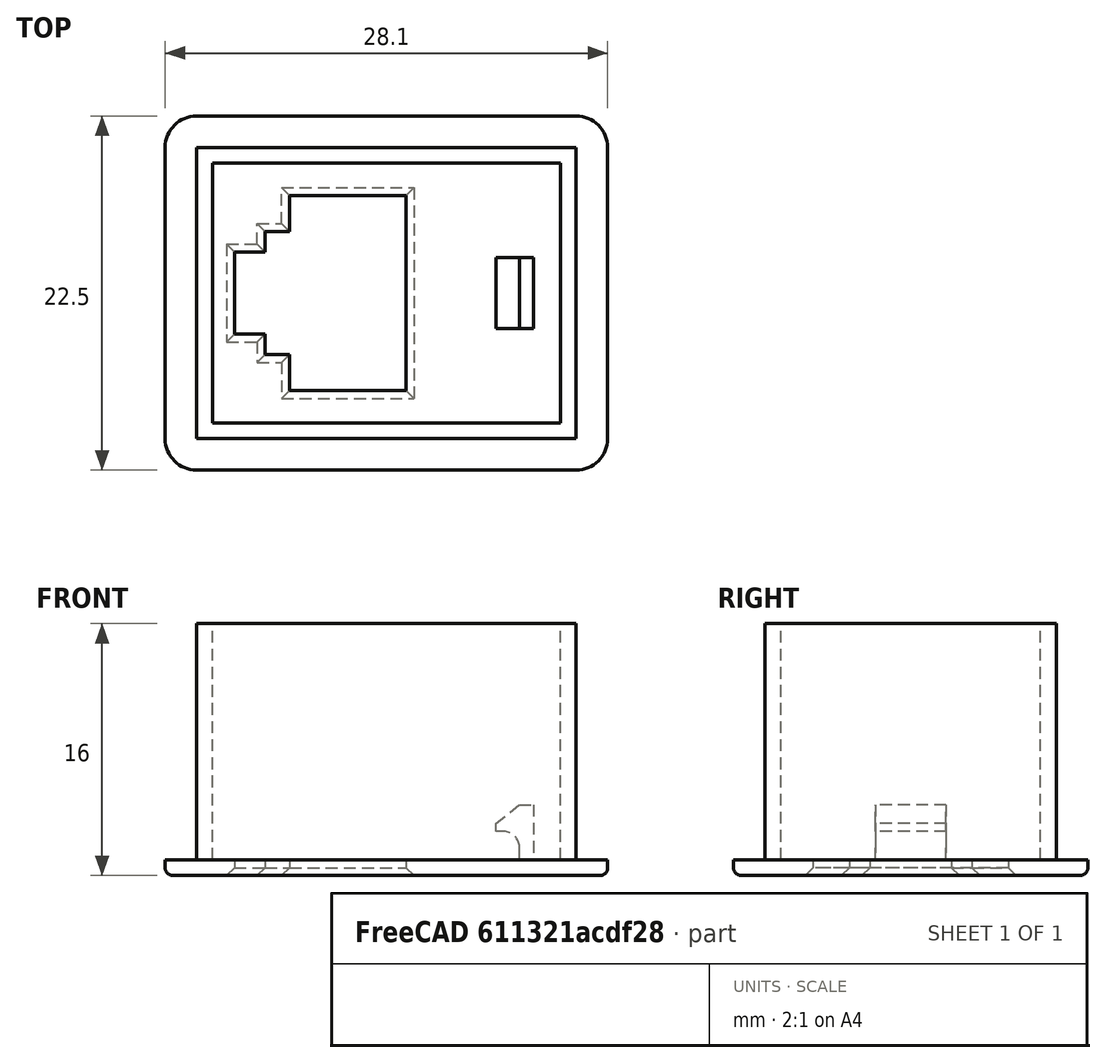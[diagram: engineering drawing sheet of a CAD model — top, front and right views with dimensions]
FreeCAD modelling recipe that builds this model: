
FCSTD DOCUMENT  (FreeCAD 0.17RUnknown)
Label: test202_lanport
License: All rights reserved
LicenseURL: http://en.wikipedia.org/wiki/All_rights_reserved
objects: Sketcher::SketchObject×5, PartDesign::Pad×3, PartDesign::Plane×2, PartDesign::Fillet×1, PartDesign::Chamfer×1, PartDesign::Body×1, Mesh::Feature×1, Mesh::Curvature×1
note: 16 computed .brp shape members not serialized (recipe doc carries the construction recipe); baked Part::Feature solids carry a one-line shape summary decoded from their .brp

FEATURE [Sketcher::SketchObject] Sketch  label="LanChanger"
  MapMode = 5
  Support = -> [XY_Plane]
  sketch-geometry (24):
    g0: LineSegment [constr] StartX=-5.25 StartY=6 StartZ=0 EndX=5.25 EndY=6 EndZ=0
    g1: LineSegment [constr] StartX=5.25 StartY=6 StartZ=0 EndX=5.25 EndY=-6 EndZ=0
    g2: LineSegment [constr] StartX=5.25 StartY=-6 StartZ=0 EndX=-5.25 EndY=-6 EndZ=0
    g3: LineSegment [constr] StartX=-5.25 StartY=-6 StartZ=0 EndX=-5.25 EndY=6 EndZ=0
    g4: LineSegment StartX=-1.75 StartY=6 StartZ=0 EndX=5.25 EndY=6 EndZ=0
    g5: LineSegment StartX=-1.75 StartY=6 StartZ=0 EndX=-1.75 EndY=3.7 EndZ=0
    g6: LineSegment StartX=-1.75 StartY=3.7 StartZ=0 EndX=-3.3 EndY=3.7 EndZ=0
    g7: LineSegment StartX=-3.3 StartY=3.7 StartZ=0 EndX=-3.3 EndY=2.4 EndZ=0
    g8: LineSegment StartX=-3.3 StartY=2.4 StartZ=0 EndX=-5.25 EndY=2.4 EndZ=0
    g9: LineSegment StartX=-1.75 StartY=-3.7 StartZ=0 EndX=-3.3 EndY=-3.7 EndZ=0
    g10: LineSegment StartX=-3.3 StartY=-3.7 StartZ=0 EndX=-3.3 EndY=-2.4 EndZ=0
    g11: LineSegment StartX=-3.3 StartY=-2.4 StartZ=0 EndX=-5.25 EndY=-2.4 EndZ=0
    g12: LineSegment StartX=-1.75 StartY=-6 StartZ=0 EndX=5.25 EndY=-6 EndZ=0
    g13: LineSegment StartX=-1.75 StartY=-6 StartZ=0 EndX=-1.75 EndY=-3.7 EndZ=0
    g14: LineSegment StartX=-5.25 StartY=-2.4 StartZ=0 EndX=-5.25 EndY=2.4 EndZ=0
    g15: LineSegment StartX=5.25 StartY=6 StartZ=0 EndX=5.25 EndY=-6 EndZ=0
    g16: LineSegment StartX=-6.65 StartY=8.05 StartZ=0 EndX=15.05 EndY=8.05 EndZ=0
    g17: LineSegment StartX=15.05 StartY=8.05 StartZ=0 EndX=15.05 EndY=-8.05 EndZ=0
    g18: LineSegment StartX=15.05 StartY=-8.05 StartZ=0 EndX=-6.65 EndY=-8.05 EndZ=0
    g19: LineSegment StartX=-6.65 StartY=-8.05 StartZ=0 EndX=-6.65 EndY=8.05 EndZ=0
    g20: LineSegment StartX=11.65 StartY=2.45 StartZ=0 EndX=13.75 EndY=2.45 EndZ=0
    g21: LineSegment StartX=13.75 StartY=2.45 StartZ=0 EndX=13.75 EndY=-2.45 EndZ=0
    g22: LineSegment StartX=13.75 StartY=-2.45 StartZ=0 EndX=11.65 EndY=-2.45 EndZ=0
    g23: LineSegment StartX=11.65 StartY=-2.45 StartZ=0 EndX=11.65 EndY=2.45 EndZ=0
  constraints (69):
    c: Coincident(g0,g1)
    c: Coincident(g1,g2)
    c: Coincident(g2,g3)
    c: Coincident(g3,g0)
    c: Horizontal(g0)
    c: Horizontal(g2)
    c: Vertical(g1)
    c: Vertical(g3)
    c: Symmetric(g0,g1,g-1)
    c: Distance(g1) = 12
    c: Distance(g0) = 10.5
    c: PointOnObject(g4,g0)
    c: Coincident(g4,g0)
    c: Distance(g4) = 7
    c: Coincident(g4,g5)
    c: Vertical(g5)
    c: Coincident(g5,g6)
    c: Horizontal(g6)
    c: Coincident(g6,g7)
    c: Vertical(g7)
    c: Coincident(g7,g8)
    c: PointOnObject(g8,g3)
    c: Horizontal(g8)
    c: Distance(g5) = 2.3
    c: Distance(g6) = 1.55
    c: Distance(g7) = 1.3
    c: Distance(g12) = 7
    c: Coincident(g12,g13)
    c: Vertical(g13)
    c: Coincident(g13,g9)
    c: Horizontal(g9)
    c: Coincident(g9,g10)
    c: Vertical(g10)
    c: Coincident(g10,g11)
    c: Horizontal(g11)
    c: Distance(g13) = 2.3
    c: Distance(g9) = 1.55
    c: Distance(g10) = 1.3
    c: Coincident(g14,g11)
    c: Coincident(g14,g8)
    c: Coincident(g15,g0)
    c: Coincident(g15,g1)
    c: Coincident(g12,g1)
    c: PointOnObject(g12,g2)
    c: PointOnObject(g14,g3)
    c: Coincident(g16,g17)
    c: Coincident(g17,g18)
    c: Coincident(g18,g19)
    c: Coincident(g19,g16)
    c: Horizontal(g16)
    c: Horizontal(g18)
    c: Vertical(g17)
    c: Vertical(g19)
    c: Symmetric(g16,g18,g-1)
    c: Distance(g16) = 21.7
    c: Distance(g8,g19) = 1.4
    c: Distance(g19) = 16.1
    c: Coincident(g20,g21)
    c: Coincident(g21,g22)
    c: Coincident(g22,g23)
    c: Coincident(g23,g20)
    c: Horizontal(g20)
    c: Horizontal(g22)
    c: Vertical(g21)
    c: Vertical(g23)
    c: Symmetric(g22,g20,g-1)
    c: Distance(g20,g17) = 1.3
    c: Distance(g20) = 2.1
    c: Distance(g21) = 4.9
FEATURE [Sketcher::SketchObject] Sketch001
  ExternalGeometry = -> [Sketch]
  MapMode = 5
  Support = -> [XY_Plane]
  sketch-geometry (8):
    g0: LineSegment StartX=-7.85 StartY=9.25 StartZ=0 EndX=16.25 EndY=9.25 EndZ=0
    g1: LineSegment StartX=16.25 StartY=9.25 StartZ=0 EndX=16.25 EndY=-9.25 EndZ=0
    g2: LineSegment StartX=16.25 StartY=-9.25 StartZ=0 EndX=-7.85 EndY=-9.25 EndZ=0
    g3: LineSegment StartX=-7.85 StartY=-9.25 StartZ=0 EndX=-7.85 EndY=9.25 EndZ=0
    g4: LineSegment StartX=-6.85 StartY=8.25 StartZ=0 EndX=15.25 EndY=8.25 EndZ=0
    g5: LineSegment StartX=15.25 StartY=8.25 StartZ=0 EndX=15.25 EndY=-8.25 EndZ=0
    g6: LineSegment StartX=15.25 StartY=-8.25 StartZ=0 EndX=-6.85 EndY=-8.25 EndZ=0
    g7: LineSegment StartX=-6.85 StartY=-8.25 StartZ=0 EndX=-6.85 EndY=8.25 EndZ=0
  constraints (24):
    c: Coincident(g0,g1)
    c: Coincident(g1,g2)
    c: Coincident(g2,g3)
    c: Coincident(g3,g0)
    c: Horizontal(g0)
    c: Horizontal(g2)
    c: Vertical(g1)
    c: Vertical(g3)
    c: Coincident(g4,g5)
    c: Coincident(g5,g6)
    c: Coincident(g6,g7)
    c: Coincident(g7,g4)
    c: Horizontal(g4)
    c: Horizontal(g6)
    c: Vertical(g5)
    c: Vertical(g7)
    c: Distance(g4,g1) = 1
    c: Symmetric(g4,g5,g-1)
    c: Distance(g-3,g4) = 0.2
    c: Distance(g-4,g7) = 0.2
    c: Distance(g-3,g5) = 0.2
    c: Distance(g4,g0) = 1
    c: Symmetric(g0,g1,g-1)
    c: Distance(g4,g3) = 1
FEATURE [PartDesign::Pad] Pad
  Length = 15
  Length2 = 100
  Profile = -> Sketch001
  Type = 0
FEATURE [Sketcher::SketchObject] Sketch002
  ExternalGeometry = -> [Pad,Sketch]
  MapMode = 5
  Placement = pos=(0,0,0) rot=(1,0,0;3.14159rad)
  Support = -> [Pad]
  sketch-geometry (20):
    g0: LineSegment StartX=-7.85 StartY=11.25 StartZ=0 EndX=16.25 EndY=11.25 EndZ=0
    g1: LineSegment StartX=18.25 StartY=9.25 StartZ=0 EndX=18.25 EndY=-9.25 EndZ=0
    g2: LineSegment StartX=16.25 StartY=-11.25 StartZ=0 EndX=-7.85 EndY=-11.25 EndZ=0
    g3: LineSegment StartX=-9.85 StartY=-9.25 StartZ=0 EndX=-9.85 EndY=9.25 EndZ=0
    g4: ArcOfCircle CenterX=-7.85 CenterY=9.25 CenterZ=0 NormalX=0 NormalY=0 NormalZ=1 AngleXU=0 Radius=2 StartAngle=1.5708 EndAngle=3.14159
    g5: ArcOfCircle CenterX=16.25 CenterY=9.25 CenterZ=0 NormalX=0 NormalY=0 NormalZ=1 AngleXU=0 Radius=2 StartAngle=0 EndAngle=1.5708
    g6: ArcOfCircle CenterX=16.25 CenterY=-9.25 CenterZ=0 NormalX=0 NormalY=0 NormalZ=1 AngleXU=0 Radius=2 StartAngle=4.71239 EndAngle=6.28319
    g7: ArcOfCircle CenterX=-7.85 CenterY=-9.25 CenterZ=0 NormalX=0 NormalY=0 NormalZ=1 AngleXU=0 Radius=2 StartAngle=3.14159 EndAngle=4.71239
    g8: LineSegment StartX=-5.45 StartY=2.6 StartZ=0 EndX=-3.5 EndY=2.6 EndZ=0
    g9: LineSegment StartX=-3.5 StartY=2.6 StartZ=0 EndX=-3.5 EndY=3.9 EndZ=0
    g10: LineSegment StartX=-3.5 StartY=3.9 StartZ=0 EndX=-1.95 EndY=3.9 EndZ=0
    g11: LineSegment StartX=-1.95 StartY=3.9 StartZ=0 EndX=-1.95 EndY=6.2 EndZ=0
    g12: LineSegment StartX=-1.95 StartY=6.2 StartZ=0 EndX=5.45 EndY=6.2 EndZ=0
    g13: LineSegment StartX=-5.45 StartY=-2.6 StartZ=0 EndX=-3.5 EndY=-2.6 EndZ=0
    g14: LineSegment StartX=-3.5 StartY=-2.6 StartZ=0 EndX=-3.5 EndY=-3.9 EndZ=0
    g15: LineSegment StartX=-3.5 StartY=-3.9 StartZ=0 EndX=-1.95 EndY=-3.9 EndZ=0
    g16: LineSegment StartX=-1.95 StartY=-3.9 StartZ=0 EndX=-1.95 EndY=-6.2 EndZ=0
    g17: LineSegment StartX=-1.95 StartY=-6.2 StartZ=0 EndX=5.45 EndY=-6.2 EndZ=0
    g18: LineSegment StartX=-5.45 StartY=-2.6 StartZ=0 EndX=-5.45 EndY=2.6 EndZ=0
    g19: LineSegment StartX=5.45 StartY=-6.2 StartZ=0 EndX=5.45 EndY=6.2 EndZ=0
  constraints (53):
    c: Horizontal(g0)
    c: Horizontal(g2)
    c: Vertical(g1)
    c: Vertical(g3)
    c: Tangent(g3,g4) = 1.5708
    c: Tangent(g0,g4) = 1.5708
    c: Tangent(g0,g5) = 1.5708
    c: Tangent(g1,g5) = 1.5708
    c: Tangent(g1,g6) = 1.5708
    c: Tangent(g2,g6) = 1.5708
    c: Tangent(g2,g7) = 1.5708
    c: Tangent(g3,g7) = 1.5708
    c: Radius(g4) = 2
    c: Equal(g4,g5)
    c: Equal(g4,g6)
    c: Equal(g4,g7)
    c: Coincident(g5,g-3)
    c: Coincident(g7,g-4)
    c: Horizontal(g8)
    c: Coincident(g8,g9)
    c: Vertical(g9)
    c: Coincident(g9,g10)
    c: Coincident(g10,g11)
    c: Coincident(g11,g12)
    c: Horizontal(g12)
    c: Vertical(g11)
    c: Horizontal(g10)
    c: Equal(g-6,g8)
    c: Equal(g10,g-5)
    c: Equal(g-8,g9)
    c: Equal(g-9,g11)
    c: DistanceX(g11,g-9) = 0.2
    c: DistanceY(g-9,g11) = 0.2
    c: Horizontal(g13)
    c: Coincident(g13,g14)
    c: Vertical(g14)
    c: Coincident(g14,g15)
    c: Coincident(g15,g16)
    c: Coincident(g16,g17)
    c: Horizontal(g17)
    c: Vertical(g16)
    c: Horizontal(g15)
    c: Equal(g-6,g13)
    c: Equal(g14,g-8)
    c: Equal(g-5,g15)
    c: Equal(g16,g-9)
    c: Coincident(g18,g13)
    c: Coincident(g18,g8)
    c: Symmetric(g8,g13,g-1)
    c: Coincident(g19,g17)
    c: Coincident(g19,g12)
    c: Vertical(g19)
    c: DistanceX(g-7,g12) = 0.2
FEATURE [PartDesign::Pad] Pad001
  BaseFeature = -> Pad
  Length = 1
  Length2 = 100
  Profile = -> Sketch002
  Type = 0
FEATURE [Sketcher::SketchObject] Sketch003
  ExternalGeometry = -> [Sketch]
  MapMode = 5
  Support = -> [Pad001]
  sketch-geometry (4):
    g0: LineSegment StartX=12.65 StartY=2.25 StartZ=0 EndX=13.55 EndY=2.25 EndZ=0
    g1: LineSegment StartX=13.55 StartY=2.25 StartZ=0 EndX=13.55 EndY=-2.25 EndZ=0
    g2: LineSegment StartX=13.55 StartY=-2.25 StartZ=0 EndX=12.65 EndY=-2.25 EndZ=0
    g3: LineSegment StartX=12.65 StartY=-2.25 StartZ=0 EndX=12.65 EndY=2.25 EndZ=0
  constraints (12):
    c: Coincident(g0,g1)
    c: Coincident(g1,g2)
    c: Coincident(g2,g3)
    c: Coincident(g3,g0)
    c: Horizontal(g0)
    c: Horizontal(g2)
    c: Vertical(g1)
    c: Vertical(g3)
    c: Symmetric(g0,g1,g-1)
    c: Distance(g1,g-6) = 0.2
    c: Distance(g0,g-3) = 0.2
    c: Distance(g2,g-4) = 1
FEATURE [PartDesign::Plane] DatumPlane
  MapMode = 1
  Placement = pos=(12.65,2.25,0) rot=(1,0,0;1.5708rad)
  Support = -> [Sketch003]
FEATURE [Sketcher::SketchObject] Sketch004
  ExternalGeometry = -> [Sketch,Sketch003]
  MapMode = 5
  Placement = pos=(12.65,2.25,0) rot=(0,0.707107,0.707107;3.14159rad)
  Support = -> [DatumPlane]
  sketch-geometry (9):
    g0: LineSegment StartX=-0.9 StartY=0 StartZ=0 EndX=0 EndY=0 EndZ=0
    g1: LineSegment StartX=0 StartY=0 StartZ=0 EndX=0 EndY=0.8 EndZ=0
    g2: LineSegment StartX=0.006483 StartY=3.5 StartZ=0 EndX=-0.9 EndY=3.5 EndZ=0
    g3: LineSegment StartX=-0.9 StartY=3.5 StartZ=0 EndX=-0.9 EndY=0 EndZ=0
    g4: LineSegment StartX=1 StartY=1.8 StartZ=0 EndX=1.5 EndY=1.8 EndZ=0
    g5: LineSegment StartX=1.5 StartY=1.8 StartZ=0 EndX=1.5 EndY=2.3 EndZ=0
    g6: LineSegment StartX=1.5 StartY=2.3 StartZ=0 EndX=0.006483 EndY=3.5 EndZ=0
    g7: LineSegment [constr] StartX=1 StartY=0 StartZ=0 EndX=1 EndY=3.22096 EndZ=0
    g8: ArcOfCircle CenterX=1 CenterY=0.8 CenterZ=0 NormalX=0 NormalY=0 NormalZ=1 AngleXU=0 Radius=1 StartAngle=1.5708 EndAngle=3.14159
  constraints (23):
    c: Coincident(g0,g1)
    c: Coincident(g2,g3)
    c: Coincident(g3,g0)
    c: Horizontal(g0)
    c: Horizontal(g2)
    c: Vertical(g1)
    c: Vertical(g3)
    c: Coincident(g0,g-5)
    c: Coincident(g-1,g0)
    c: Distance(g3) = 3.5
    c: Horizontal(g4)
    c: Coincident(g4,g5)
    c: Vertical(g5)
    c: Coincident(g5,g6)
    c: Coincident(g6,g2)
    c: Coincident(g7,g-3)
    c: Vertical(g7)
    c: Tangent(g1,g8) = 1.5708
    c: Tangent(g4,g8) = 1.5708
    c: Radius(g8) = 1
    c: Distance(g5,g7) = 0.5
    c: Equal(g4,g5)
    c: DistanceY(g7,g4) = 1.8
FEATURE [PartDesign::Plane] DatumPlane001
  MapMode = 7
  Placement = pos=(12.65,-2.25,0) rot=(1,0,0;1.5708rad)
  Support = -> [Sketch003]
FEATURE [PartDesign::Pad] Pad002
  BaseFeature = -> Pad001
  Length = 4.5
  Length2 = 100
  Profile = -> Sketch004
  Reversed = true
  Type = 3
  UpToFace = -> DatumPlane001 [Plane]
FEATURE [PartDesign::Fillet] Fillet
  Base = -> Pad002 [Edge57]
  BaseFeature = -> Pad002
  Radius = 0.5
FEATURE [PartDesign::Chamfer] Chamfer
  Base = -> Fillet [Edge38,Edge37,Edge36,Edge35,Edge34,Edge33,Edge44,Edge43,Edge42,Edge41,Edge40,Edge39]
  BaseFeature = -> Fillet
  Size = 0.5
FEATURE [PartDesign::Body] Body
  Group = -> [Sketch,Sketch001,Pad,Sketch002,Pad001,Sketch003,DatumPlane,Sketch004,Pad002,DatumPlane001,Fillet,Chamfer]
  Origin = -> Origin
  Tip = -> Chamfer
FEATURE [Mesh::Feature] Mesh  label="Chamfer (Meshed)"
FEATURE [Mesh::Curvature] Mesh_Curvature
  Source = -> Mesh
